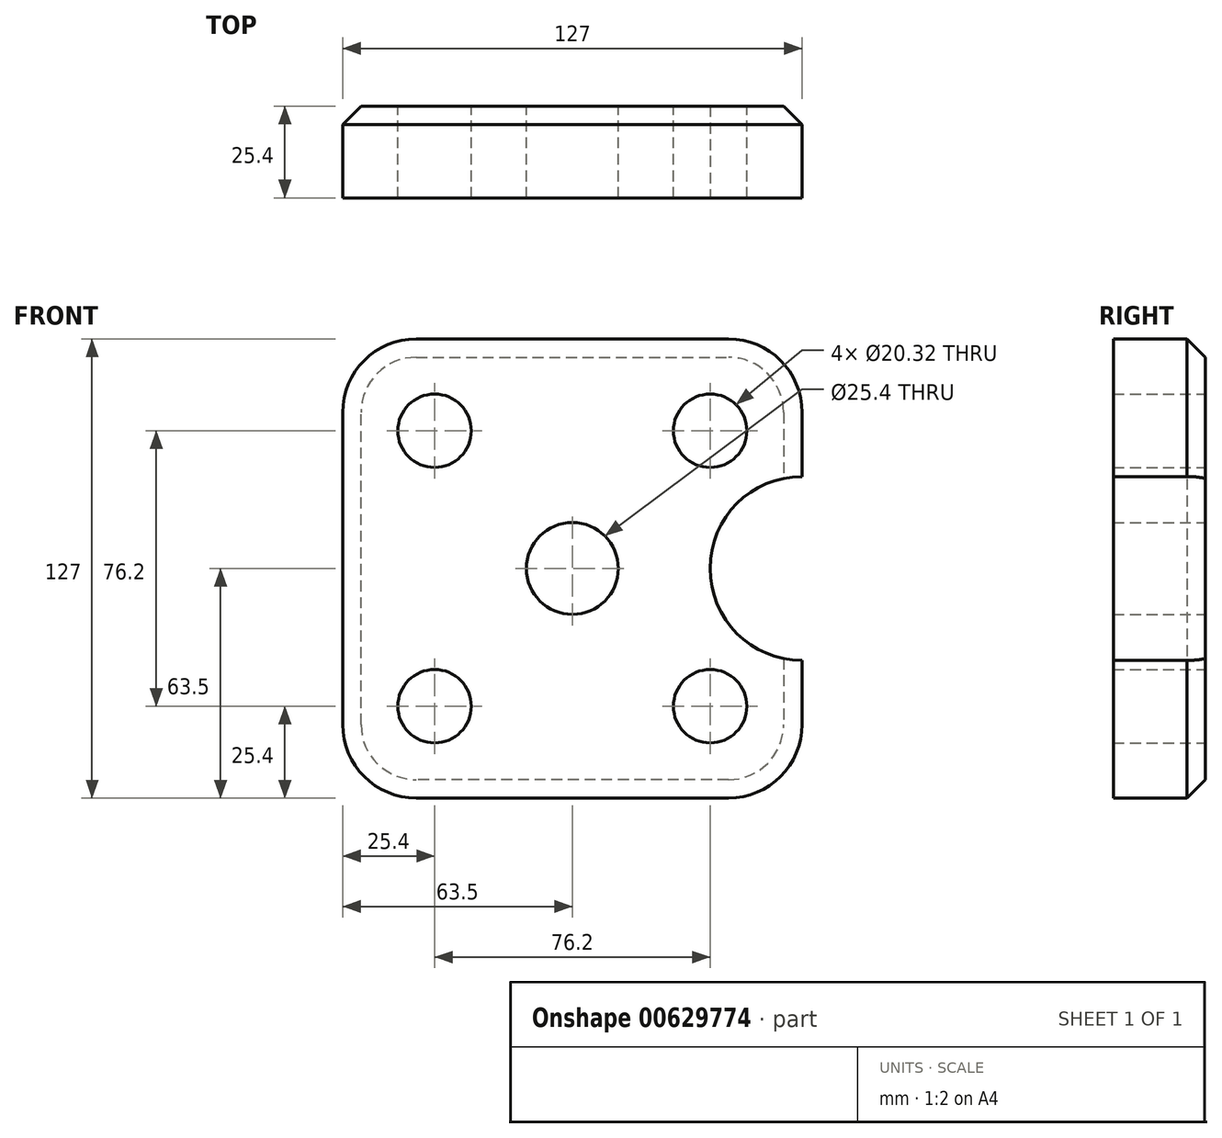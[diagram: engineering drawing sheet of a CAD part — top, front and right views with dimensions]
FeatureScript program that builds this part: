
annotation { "Feature Type Name" : "Feature", "Feature Type Description" : "" }
export const myFeature = defineFeature(function(context is Context, id is Id, definition is map)
    precondition{}
    {
        {
            var Q0;
            Q0=qCreatedBy(makeId("Front.planeOp"),FACE);
            var sketch = newSketch(context, id + "F0", { "sketchPlane" : qUnion([Q0])});
            skLineSegment(sketch, "E0.bottom", {"start": v(-63.5, -63.5) * mm, "end": v(63.5, -63.5) * mm});
            skLineSegment(sketch, "E0.top", {"start": v(-63.5, 63.5) * mm, "end": v(63.5, 63.5) * mm});
            skLineSegment(sketch, "E0.left", {"start": v(-63.5, -63.5) * mm, "end": v(-63.5, 63.5) * mm});
            skLineSegment(sketch, "E0.right", {"start": v(63.5, -63.5) * mm, "end": v(63.5, 63.5) * mm});
            skPoint(sketch, "E0.middle", {"position": v(0, 0) * mm});
            skCircle(sketch, "E1", {"center": v(0, 0) * mm, "radius": 12.7 * mm});
            skCircle(sketch, "E2", {"center": v(-38.1, 38.1) * mm, "radius": 10.16 * mm});
            skCircle(sketch, "E3.0.1.0", {"center": v(-38.1, -38.1) * mm, "radius": 10.16 * mm});
            skCircle(sketch, "E3.1.0.0", {"center": v(38.1, 38.1) * mm, "radius": 10.16 * mm});
            skCircle(sketch, "E3.1.1.0", {"center": v(38.1, -38.1) * mm, "radius": 10.16 * mm});
            skLineSegment(sketch, "E3.direction1", {"start": v(-38.1, 38.1) * mm, "end": v(38.1, 38.1) * mm, "construction": true});
            skLineSegment(sketch, "E3.direction2", {"start": v(-38.1, 38.1) * mm, "end": v(-38.1, -38.1) * mm, "construction": true});
            skSolve(sketch);
        }
        {
            var Q0;
            Q0=makeQuery(id+"F0.imprint","IMPRINT",FACE,{"disambiguationData":[TD([[makeQuery(id+"F0.imprint","IMPRINT",EDGE,{"derivedFrom":sQuery(id+"F0.wireOp",EDGE,"E0.bottom")}),1.0]])]});
            extrude(context, id + "F1", {"entities" : qUnion([Q0]), "depth" : 25.4 * mm, "offsetDistance" : 25.4 * mm});
        }
        {
            var Q0;
            Q0=makeQuery(id+"F1.opExtrude","SWEPT_EDGE",EDGE,{"disambiguationData":[OSD([sQuery(id+"F0.wireOp",EDGE,"E0.top"),sQuery(id+"F0.wireOp",EDGE,"E0.right")])]});
            var Q1;
            Q1=makeQuery(id+"F1.opExtrude","SWEPT_EDGE",EDGE,{"disambiguationData":[OSD([sQuery(id+"F0.wireOp",EDGE,"E0.top"),sQuery(id+"F0.wireOp",EDGE,"E0.left")])]});
            var Q2;
            Q2=makeQuery(id+"F1.opExtrude","SWEPT_EDGE",EDGE,{"disambiguationData":[OSD([sQuery(id+"F0.wireOp",EDGE,"E0.bottom"),sQuery(id+"F0.wireOp",EDGE,"E0.right")])]});
            var Q3;
            Q3=makeQuery(id+"F1.opExtrude","SWEPT_EDGE",EDGE,{"disambiguationData":[OSD([sQuery(id+"F0.wireOp",EDGE,"E0.bottom"),sQuery(id+"F0.wireOp",EDGE,"E0.left")])]});
            fillet(context, id + "F2", {"entities" : qUnion([Q0, Q1, Q2, Q3]), "radius" : 20.32 * mm, "tangentPropagation" : true, "allowEdgeOverflow" : false});
        }
        {
            var Q0;
            Q0=makeQuery(id+"F1.opExtrude","CAP_EDGE",EDGE,{"disambiguationData":[OSD([sQuery(id+"F0.wireOp",EDGE,"E0.bottom")])],"isStart":true});
            chamfer(context, id + "F3", {"entities" : qUnion([Q0]), "width" : 5.08 * mm, "tangentPropagation" : true});
        }
        {
            var Q0;
            Q0=makeQuery(id+"F1.opExtrude","CAP_FACE",FACE,{"disambiguationData":[OSD([sQuery(id+"F0.wireOp",EDGE,"E0.bottom"),sQuery(id+"F0.wireOp",EDGE,"E0.top"),sQuery(id+"F0.wireOp",EDGE,"E0.left"),sQuery(id+"F0.wireOp",EDGE,"E0.right"),sQuery(id+"F0.wireOp",EDGE,"E1"),sQuery(id+"F0.wireOp",EDGE,"E2"),sQuery(id+"F0.wireOp",EDGE,"E3.0.1.0"),sQuery(id+"F0.wireOp",EDGE,"E3.1.0.0"),sQuery(id+"F0.wireOp",EDGE,"E3.1.1.0")])],"isStart":false});
            var sketch = newSketch(context, id + "F4", { "sketchPlane" : qUnion([Q0])});
            skCircle(sketch, "E4", {"center": v(63.5, 0) * mm, "radius": 25.44 * mm});
            skSolve(sketch);
        }
        {
            var Q0;
            {var subQ0=sQuery(id+"F4.wireOp",EDGE,"E4");var subQ1=makeQuery(id+"F1.opExtrude","CAP_EDGE",EDGE,{"disambiguationData":[OSD([sQuery(id+"F0.wireOp",EDGE,"E0.right")])],"isStart":false});var subQ2=makeQuery(id+"F4.imprint","INTERSECT",VERTEX,{"disambiguationData":[OD(0.0)],"derivedFrom":[subQ1,subQ0]});Q0=makeQuery(id+"F4.imprint","IMPRINT",FACE,{"disambiguationData":[TD([[makeQuery(id+"F4.imprint","IMPRINT",EDGE,{"disambiguationData":[TD([[subQ2,1.0]])],"derivedFrom":subQ0}),1.0]])]});}
            extrude(context, id + "F5", {"entities" : qUnion([Q0]), "operationType" : NewBodyOperationType.REMOVE, "oppositeDirection" : true, "depth" : 50.9 * mm, "offsetDistance" : 25.4 * mm});
        }
    });
